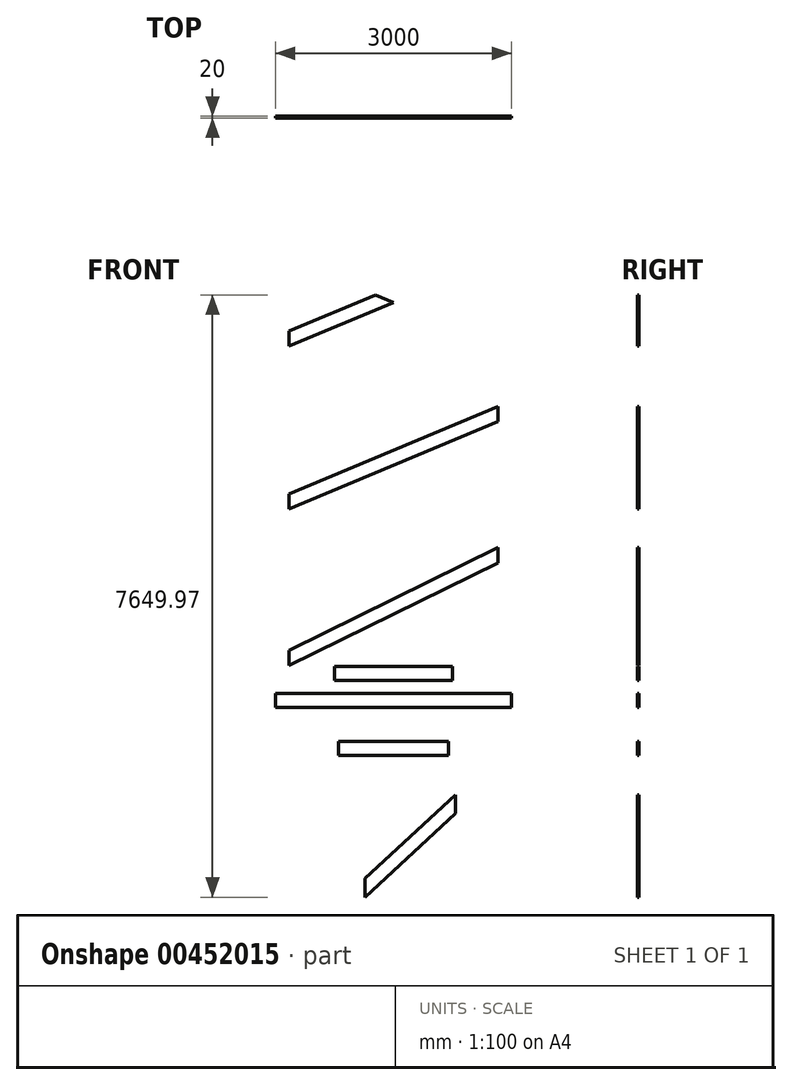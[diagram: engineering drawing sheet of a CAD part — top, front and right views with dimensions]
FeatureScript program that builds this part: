
annotation { "Feature Type Name" : "Feature", "Feature Type Description" : "" }
export const myFeature = defineFeature(function(context is Context, id is Id, definition is map)
    precondition{}
    {
        {
            var Q0;
            Q0=qCreatedBy(makeId("Front.planeOp"),FACE);
            var sketch = newSketch(context, id + "F0", { "sketchPlane" : qUnion([Q0])});
            skLineSegment(sketch, "E0.bottom", {"start": v(1500, 87.5) * mm, "end": v(-1500, 87.5) * mm});
            skLineSegment(sketch, "E0.top", {"start": v(1500, -87.5) * mm, "end": v(-1500, -87.5) * mm});
            skLineSegment(sketch, "E0.left", {"start": v(1500, 87.5) * mm, "end": v(1500, -87.5) * mm});
            skLineSegment(sketch, "E0.right", {"start": v(-1500, 87.5) * mm, "end": v(-1500, -87.5) * mm});
            skPoint(sketch, "E0.middle", {"position": v(0, 0) * mm});
            skLineSegment(sketch, "E1.bottom", {"start": v(750, 255.3) * mm, "end": v(-750, 255.3) * mm});
            skLineSegment(sketch, "E1.top", {"start": v(750, 430.3) * mm, "end": v(-750, 430.3) * mm});
            skLineSegment(sketch, "E1.left", {"start": v(750, 255.3) * mm, "end": v(750, 430.3) * mm});
            skLineSegment(sketch, "E1.right", {"start": v(-750, 255.3) * mm, "end": v(-750, 430.3) * mm});
            skPoint(sketch, "E1.middle", {"position": v(0, 342.8) * mm});
            skPoint(sketch, "E1.middle.positionSnap0", {"position": v(0, 87.5) * mm});
            skPoint(sketch, "E1.centerSnap0", {"position": v(0, 87.5) * mm});
            skLineSegment(sketch, "E2.bottom", {"start": v(1325, 1942.33) * mm, "end": v(-1325, 1942.33) * mm, "construction": true});
            skLineSegment(sketch, "E2.top", {"start": v(1325, 442.33) * mm, "end": v(-1325, 442.33) * mm, "construction": true});
            skLineSegment(sketch, "E2.left", {"start": v(1325, 1942.33) * mm, "end": v(1325, 442.33) * mm, "construction": true});
            skLineSegment(sketch, "E2.right", {"start": v(-1325, 1942.33) * mm, "end": v(-1325, 442.33) * mm, "construction": true});
            skPoint(sketch, "E2.middle", {"position": v(0, 1192.33) * mm});
            skLineSegment(sketch, "E3", {"start": v(1325, 1942.33) * mm, "end": v(-1325, 637.4) * mm});
            skLineSegment(sketch, "E4", {"start": v(-1325, 637.4) * mm, "end": v(-1325, 442.33) * mm});
            skLineSegment(sketch, "E5", {"start": v(-1325, 442.33) * mm, "end": v(1325, 1747.27) * mm});
            skLineSegment(sketch, "E6", {"start": v(1325, 1747.27) * mm, "end": v(1325, 1942.33) * mm});
            skLineSegment(sketch, "E7.bottom", {"start": v(1325, 2432.05) * mm, "end": v(-1325, 2432.05) * mm, "construction": true});
            skLineSegment(sketch, "E7.top", {"start": v(1325, 3732.05) * mm, "end": v(-1325, 3732.05) * mm, "construction": true});
            skLineSegment(sketch, "E7.left", {"start": v(1325, 2432.05) * mm, "end": v(1325, 3732.05) * mm, "construction": true});
            skLineSegment(sketch, "E7.right", {"start": v(-1325, 2432.05) * mm, "end": v(-1325, 3732.05) * mm, "construction": true});
            skPoint(sketch, "E7.middle", {"position": v(0, 3082.05) * mm});
            skPoint(sketch, "E7.middle.positionSnap0", {"position": v(0, 1942.33) * mm});
            skPoint(sketch, "E7.centerSnap0", {"position": v(0, 1942.33) * mm});
            skLineSegment(sketch, "E8", {"start": v(1325, 3732.05) * mm, "end": v(-1325, 2621.8) * mm});
            skLineSegment(sketch, "E9", {"start": v(-1325, 2621.8) * mm, "end": v(-1325, 2432.05) * mm});
            skLineSegment(sketch, "E10", {"start": v(-1325, 2432.05) * mm, "end": v(1325, 3542.31) * mm});
            skLineSegment(sketch, "E11", {"start": v(1325, 3542.31) * mm, "end": v(1325, 3732.05) * mm});
            skLineSegment(sketch, "E12.bottom", {"start": v(700, -520.98) * mm, "end": v(-700, -520.98) * mm});
            skLineSegment(sketch, "E12.top", {"start": v(700, -695.98) * mm, "end": v(-700, -695.98) * mm});
            skLineSegment(sketch, "E12.left", {"start": v(700, -520.98) * mm, "end": v(700, -695.98) * mm});
            skLineSegment(sketch, "E12.right", {"start": v(-700, -520.98) * mm, "end": v(-700, -695.98) * mm});
            skPoint(sketch, "E12.middle", {"position": v(0, -608.48) * mm});
            skLineSegment(sketch, "E13.bottom", {"start": v(1325, 5800) * mm, "end": v(-1325, 5800) * mm, "construction": true});
            skLineSegment(sketch, "E13.top", {"start": v(1325, 4500) * mm, "end": v(-1325, 4500) * mm, "construction": true});
            skLineSegment(sketch, "E13.left", {"start": v(1325, 5800) * mm, "end": v(1325, 4500) * mm, "construction": true});
            skLineSegment(sketch, "E13.right", {"start": v(-1325, 5800) * mm, "end": v(-1325, 4500) * mm, "construction": true});
            skPoint(sketch, "E13.middle", {"position": v(0, 5150) * mm});
            skPoint(sketch, "E13.middle.positionSnap0", {"position": v(0, 3732.05) * mm});
            skPoint(sketch, "E13.centerSnap0", {"position": v(0, 3732.05) * mm});
            skLineSegment(sketch, "E14", {"start": v(1325, 4500) * mm, "end": v(-1325, 5610.26) * mm, "construction": true});
            skLineSegment(sketch, "E15", {"start": v(-1325, 5610.26) * mm, "end": v(-1325, 5800) * mm, "construction": true});
            skLineSegment(sketch, "E16", {"start": v(-1325, 5800) * mm, "end": v(1325, 4689.74) * mm, "construction": true});
            skLineSegment(sketch, "E17", {"start": v(1325, 4689.74) * mm, "end": v(1325, 4500) * mm, "construction": true});
            skLineSegment(sketch, "E18", {"start": v(-1325, 4500) * mm, "end": v(0, 5055.13) * mm});
            skLineSegment(sketch, "E19", {"start": v(0, 5055.13) * mm, "end": v(-226.44, 5150) * mm});
            skLineSegment(sketch, "E20", {"start": v(-226.44, 5150) * mm, "end": v(-1325, 4689.74) * mm});
            skLineSegment(sketch, "E21", {"start": v(-1325, 4689.74) * mm, "end": v(-1325, 4500) * mm});
            skLineSegment(sketch, "E22.bottom", {"start": v(787.06, -1199.97) * mm, "end": v(-362.94, -1199.97) * mm, "construction": true});
            skLineSegment(sketch, "E22.top", {"start": v(787.06, -2499.97) * mm, "end": v(-362.94, -2499.97) * mm, "construction": true});
            skLineSegment(sketch, "E22.left", {"start": v(787.06, -1199.97) * mm, "end": v(787.06, -2499.97) * mm, "construction": true});
            skLineSegment(sketch, "E22.right", {"start": v(-362.94, -1199.97) * mm, "end": v(-362.94, -2499.97) * mm, "construction": true});
            skPoint(sketch, "E22.middle", {"position": v(212.06, -1849.97) * mm});
            skLineSegment(sketch, "E23", {"start": v(787.06, -1199.97) * mm, "end": v(-362.94, -2261.79) * mm});
            skLineSegment(sketch, "E24", {"start": v(-362.94, -2261.79) * mm, "end": v(-362.94, -2499.97) * mm});
            skLineSegment(sketch, "E25", {"start": v(-362.94, -2499.97) * mm, "end": v(787.06, -1438.16) * mm});
            skLineSegment(sketch, "E26", {"start": v(787.06, -1438.16) * mm, "end": v(787.06, -1199.97) * mm});
            skSolve(sketch);
        }
        {
            var Q0;
            Q0 = qSketchRegion(id + "F0", true);
            extrude(context, id + "F1", {"entities" : qUnion([Q0]), "depth" : 20 * mm});
        }
    });
